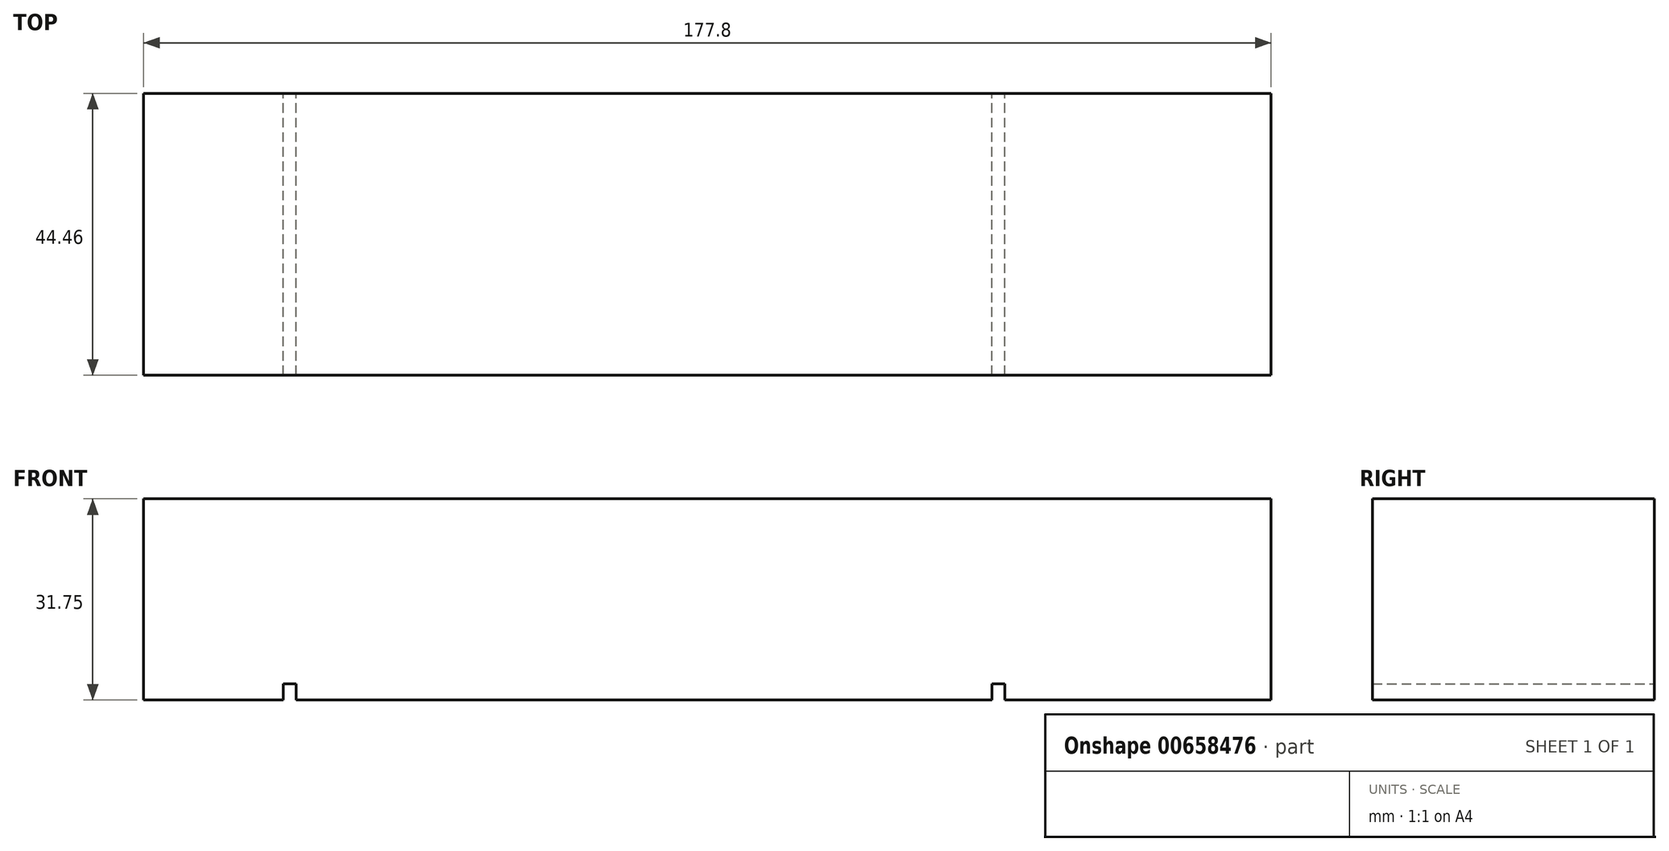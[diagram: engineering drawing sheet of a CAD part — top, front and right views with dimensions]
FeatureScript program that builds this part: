
annotation { "Feature Type Name" : "Feature", "Feature Type Description" : "" }
export const myFeature = defineFeature(function(context is Context, id is Id, definition is map)
    precondition{}
    {
        {
            var Q0;
            Q0=qCreatedBy(makeId("Top.planeOp"),FACE);
            var sketch = newSketch(context, id + "F0", { "sketchPlane" : qUnion([Q0])});
            skLineSegment(sketch, "E0.bottom", {"start": v(88.9, -22.22) * mm, "end": v(-88.9, -22.23) * mm});
            skLineSegment(sketch, "E0.top", {"start": v(88.9, 22.23) * mm, "end": v(-88.9, 22.22) * mm});
            skLineSegment(sketch, "E0.left", {"start": v(88.9, -22.22) * mm, "end": v(88.9, 22.23) * mm});
            skLineSegment(sketch, "E0.right", {"start": v(-88.9, -22.23) * mm, "end": v(-88.9, 22.22) * mm});
            skPoint(sketch, "E0.middle", {"position": v(0, 0) * mm});
            skSolve(sketch);
        }
        {
            var Q0;
            Q0=makeQuery(id+"F0.imprint","IMPRINT",FACE,{"disambiguationData":[TD([[makeQuery(id+"F0.imprint","IMPRINT",EDGE,{"derivedFrom":sQuery(id+"F0.wireOp",EDGE,"E0.bottom")}),-1.0]])]});
            extrude(context, id + "F1", {"entities" : qUnion([Q0]), "depth" : 31.75 * mm});
        }
        {
            var Q0;
            Q0=qCreatedBy(makeId("Front.planeOp"),FACE);
            var sketch = newSketch(context, id + "F2", { "sketchPlane" : qUnion([Q0])});
            skLineSegment(sketch, "E1.bottom", {"start": v(-64.87, 2.54) * mm, "end": v(-66.9, 2.54) * mm});
            skLineSegment(sketch, "E1.top", {"start": v(-64.87, -2.54) * mm, "end": v(-66.9, -2.54) * mm});
            skLineSegment(sketch, "E1.left", {"start": v(-64.87, 2.54) * mm, "end": v(-64.87, -2.54) * mm});
            skLineSegment(sketch, "E1.right", {"start": v(-66.9, 2.54) * mm, "end": v(-66.9, -2.54) * mm});
            skPoint(sketch, "E1.middle", {"position": v(-65.89, 0) * mm});
            skLineSegment(sketch, "E2.bottom", {"start": v(46.89, 2.54) * mm, "end": v(44.86, 2.54) * mm});
            skLineSegment(sketch, "E2.top", {"start": v(46.89, -0.42) * mm, "end": v(44.86, -0.42) * mm});
            skLineSegment(sketch, "E2.left", {"start": v(46.89, 2.54) * mm, "end": v(46.89, -0.42) * mm});
            skLineSegment(sketch, "E2.right", {"start": v(44.86, 2.54) * mm, "end": v(44.86, -0.42) * mm});
            skPoint(sketch, "E2.middle", {"position": v(45.87, 1.06) * mm});
            skSolve(sketch);
        }
        {
            var Q0;
            Q0=makeQuery(id+"F2.imprint","IMPRINT",FACE,{"disambiguationData":[TD([[makeQuery(id+"F2.imprint","IMPRINT",EDGE,{"derivedFrom":sQuery(id+"F2.wireOp",EDGE,"E1.bottom")}),1.0]])]});
            var Q1;
            Q1=makeQuery(id+"F2.imprint","IMPRINT",FACE,{"disambiguationData":[TD([[makeQuery(id+"F2.imprint","IMPRINT",EDGE,{"derivedFrom":sQuery(id+"F2.wireOp",EDGE,"E2.bottom")}),1.0]])]});
            extrude(context, id + "F3", {"entities" : qUnion([Q0, Q1]), "operationType" : NewBodyOperationType.REMOVE, "endBound" : BoundingType.SYMMETRIC, "depth" : 141.73 * mm});
        }
    });
